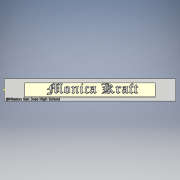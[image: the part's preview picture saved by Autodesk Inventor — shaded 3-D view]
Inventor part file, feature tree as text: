
AUTODESK INVENTOR PART (.ipt)
format: ipt  version: 2018 (Build 220112000, 112)  size: 2,807,296 bytes
history: native  units: in
note: dims shown in document units (in); Inventor stores cm internally (conversion verified against a paired STEP export)
features: sketch x8, extrude x7
ambient origin geometry x8: Origin, YZ Plane, XZ Plane, XY Plane, X Axis, Y Axis, Z Axis, Center Point
bodies: Solid1 (feature_tree)
feature tree (15):
  extrude  "Extrusion1"  Depth=0.009in TaperAngle=0.0deg
  extrude  "Extrusion2"  Depth=0.009in TaperAngle=0.0deg
  sketch  "Sketch3"  dims[d8=0.009in d9=0.0in d10=0.009in d11=0.0in]
  extrude  "Extrusion3"  Depth=0.009in TaperAngle=0.0deg
  extrude  "Extrusion4"  [1 undecoded]
  extrude  "Extrusion5"  [1 undecoded]
  sketch  "Sketch7"
  sketch  "Sketch8"
  extrude  "Extrusion6"  [1 undecoded]
  extrude  "Extrusion7"  [1 undecoded]
  sketch  "Sketch1"  dims[d0=3.0in d1=0.0in d2=0.009in d3=0.0in]
  sketch  "Sketch2"  dims[d4=0.01in d5=0.0in d6=0.009in d7=0.0in]
  sketch  "Sketch4"  dims[d12=0.009in d13=0.0in]
  sketch  "Sketch5"
  sketch  "Sketch6"
note: 4 required parameter values undecoded (feature->parameter linkage not recoverable at this tier; creation-order binding heuristic only, values carry confidence <= 0.55)
